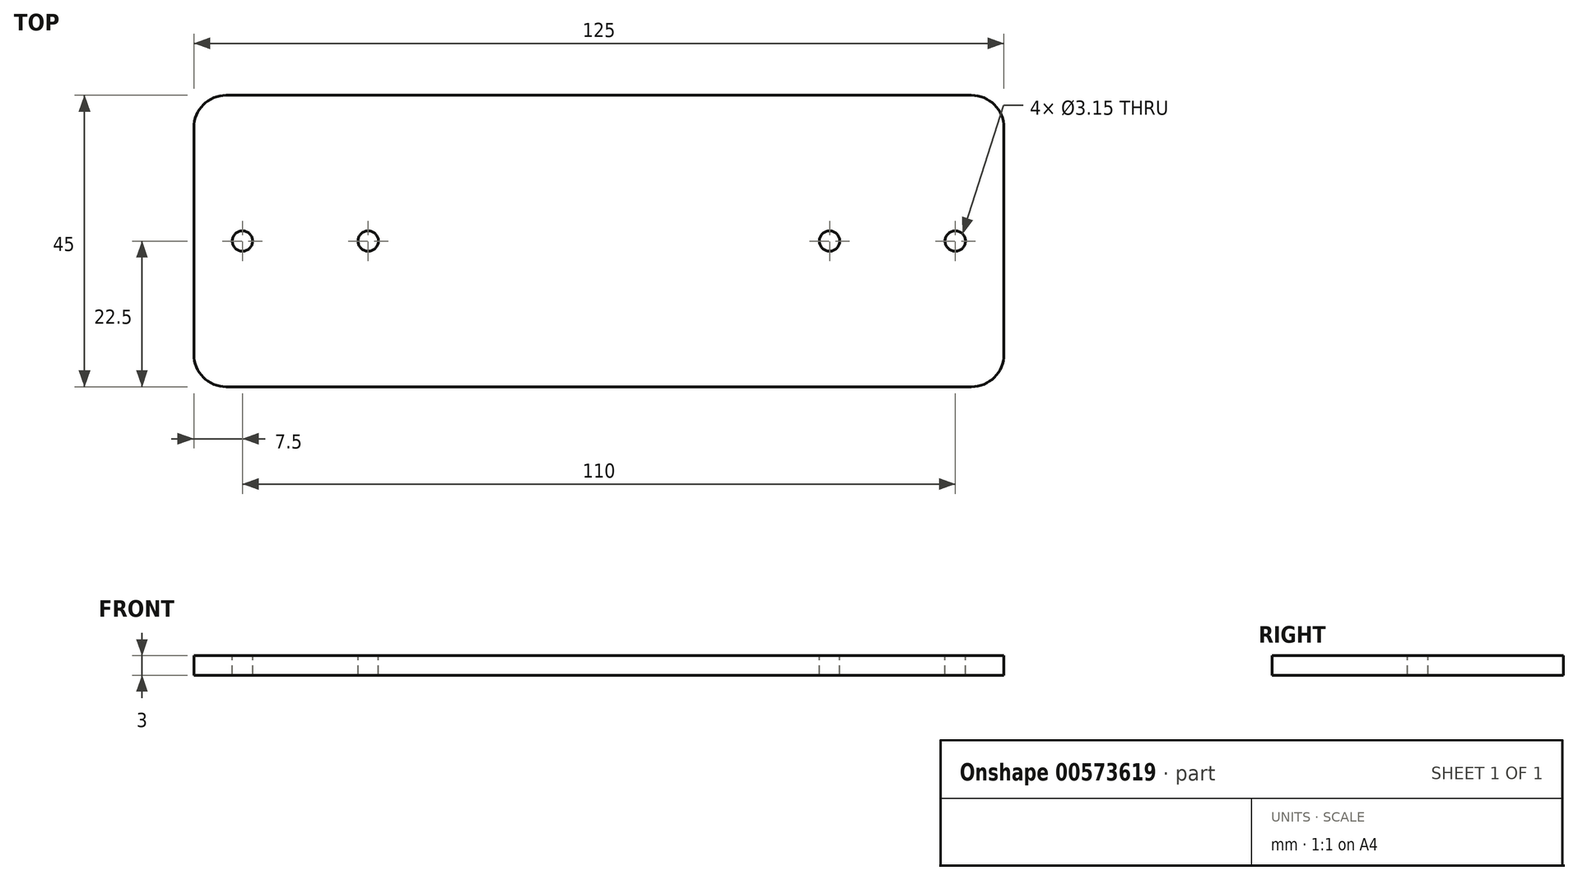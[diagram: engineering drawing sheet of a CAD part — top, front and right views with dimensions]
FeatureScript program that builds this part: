
annotation { "Feature Type Name" : "Feature", "Feature Type Description" : "" }
export const myFeature = defineFeature(function(context is Context, id is Id, definition is map)
    precondition{}
    {
        {
            var Q0;
            Q0=qCreatedBy(makeId("Top.planeOp"),FACE);
            var sketch = newSketch(context, id + "F0", { "sketchPlane" : qUnion([Q0])});
            skLineSegment(sketch, "E0.bottom", {"start": v(62.5, -22.5) * mm, "end": v(-62.5, -22.5) * mm});
            skLineSegment(sketch, "E0.top", {"start": v(62.5, 22.5) * mm, "end": v(-62.5, 22.5) * mm});
            skLineSegment(sketch, "E0.left", {"start": v(62.5, -22.5) * mm, "end": v(62.5, 22.5) * mm});
            skLineSegment(sketch, "E0.right", {"start": v(-62.5, -22.5) * mm, "end": v(-62.5, 22.5) * mm});
            skPoint(sketch, "E0.middle", {"position": v(0, 0) * mm});
            skSolve(sketch);
        }
        {
            var Q0;
            Q0 = qSketchRegion(id + "F0", true);
            extrude(context, id + "F1", {"entities" : qUnion([Q0]), "depth" : 3 * mm, "offsetDistance" : 25 * mm});
        }
        {
            var Q0;
            Q0=makeQuery(id+"F1.opExtrude","CAP_FACE",FACE,{"disambiguationData":[OSD([sQuery(id+"F0.wireOp",EDGE,"E0.bottom"),sQuery(id+"F0.wireOp",EDGE,"E0.top"),sQuery(id+"F0.wireOp",EDGE,"E0.left"),sQuery(id+"F0.wireOp",EDGE,"E0.right")])],"isStart":false});
            var sketch = newSketch(context, id + "F2", { "sketchPlane" : qUnion([Q0])});
            skLineSegment(sketch, "E1.bottom", {"start": v(-50.8, 22.5) * mm, "end": v(-37.8, 22.5) * mm});
            skLineSegment(sketch, "E1.top", {"start": v(-50.8, -22.5) * mm, "end": v(-37.8, -22.5) * mm});
            skLineSegment(sketch, "E1.left", {"start": v(-50.8, 22.5) * mm, "end": v(-50.8, -22.5) * mm});
            skLineSegment(sketch, "E1.right", {"start": v(-37.8, 22.5) * mm, "end": v(-37.8, -22.5) * mm});
            skLineSegment(sketch, "E2.bottom", {"start": v(37.8, 22.5) * mm, "end": v(50.8, 22.5) * mm});
            skLineSegment(sketch, "E2.top", {"start": v(37.8, -22.5) * mm, "end": v(50.8, -22.5) * mm});
            skLineSegment(sketch, "E2.left", {"start": v(37.8, 22.5) * mm, "end": v(37.8, -22.5) * mm});
            skLineSegment(sketch, "E2.right", {"start": v(50.8, 22.5) * mm, "end": v(50.8, -22.5) * mm});
            skLineSegment(sketch, "E3", {"start": v(-37.8, 0) * mm, "end": v(37.8, 0) * mm, "construction": true});
            skPoint(sketch, "E4", {"position": v(0, 0) * mm});
            skLineSegment(sketch, "E5", {"start": v(0, 22.5) * mm, "end": v(0, -22.5) * mm, "construction": true});
            skPoint(sketch, "E6", {"position": v(0, -22.5) * mm});
            skSolve(sketch);
        }
        {
            var Q0;
            {var subQ0=sQuery(id+"F2.wireOp",EDGE,"E1.right");Q0=makeQuery(id+"F2.imprint","IMPRINT",FACE,{"disambiguationData":[TD([[makeQuery(id+"F2.imprint","IMPRINT",EDGE,{"derivedFrom":subQ0}),1.0]])]});}
            var sketch = newSketch(context, id + "F3", { "sketchPlane" : qUnion([Q0])});
            skCircle(sketch, "E7", {"center": v(-55, 0) * mm, "radius": 1.57 * mm});
            skCircle(sketch, "E8", {"center": v(-35.6, 0) * mm, "radius": 1.57 * mm});
            skLineSegment(sketch, "E9", {"start": v(-55, 0) * mm, "end": v(-35.6, 0) * mm, "construction": true});
            skLineSegment(sketch, "E10", {"start": v(-45.3, 22.5) * mm, "end": v(-45.3, -22.5) * mm, "construction": true});
            skPoint(sketch, "E11", {"position": v(-45.3, 0) * mm});
            skPoint(sketch, "E11.positionSnap0", {"position": v(-45.3, 0) * mm});
            skCircle(sketch, "E12", {"center": v(-55, 0) * mm, "radius": 2.2 * mm, "construction": true});
            skCircle(sketch, "E13", {"center": v(-35.6, 0) * mm, "radius": 2.2 * mm, "construction": true});
            skLineSegment(sketch, "E14", {"start": v(0, 22.63) * mm, "end": v(0, -22.3) * mm, "construction": true});
            skPoint(sketch, "E15.MirrorP", {"position": v(45.3, 0) * mm});
            skCircle(sketch, "E16.MirrorC", {"center": v(55, 0) * mm, "radius": 1.57 * mm});
            skCircle(sketch, "E17.MirrorC", {"center": v(35.6, 0) * mm, "radius": 1.57 * mm});
            skLineSegment(sketch, "E18.MirrorCS", {"start": v(45.3, 22.5) * mm, "end": v(45.3, -22.5) * mm, "construction": true});
            skLineSegment(sketch, "E19.MirrorCS", {"start": v(55, 0) * mm, "end": v(35.6, 0) * mm, "construction": true});
            skCircle(sketch, "E20.MirrorC", {"center": v(55, 0) * mm, "radius": 2.2 * mm, "construction": true});
            skCircle(sketch, "E21.MirrorC", {"center": v(35.6, 0) * mm, "radius": 2.2 * mm, "construction": true});
            skSolve(sketch);
        }
        {
            var Q0;
            Q0 = qSketchRegion(id + "F3", true);
            var Q1;
            Q1=makeQuery(id+"F1.opExtrude","CAP_FACE",FACE,{"disambiguationData":[OSD([sQuery(id+"F0.wireOp",EDGE,"E0.bottom"),sQuery(id+"F0.wireOp",EDGE,"E0.top"),sQuery(id+"F0.wireOp",EDGE,"E0.left"),sQuery(id+"F0.wireOp",EDGE,"E0.right")])],"isStart":true});
            extrude(context, id + "F4", {"entities" : qUnion([Q0]), "operationType" : NewBodyOperationType.REMOVE, "endBound" : BoundingType.UP_TO_SURFACE, "oppositeDirection" : true, "depth" : 25 * mm, "endBoundEntityFace" : qUnion([Q1]), "offsetDistance" : 25 * mm});
        }
        {
            var Q0;
            Q0=makeQuery(id+"F1.opExtrude","SWEPT_EDGE",EDGE,{"disambiguationData":[OSD([sQuery(id+"F0.wireOp",EDGE,"E0.bottom"),sQuery(id+"F0.wireOp",EDGE,"E0.right")])]});
            var Q1;
            Q1=makeQuery(id+"F1.opExtrude","SWEPT_EDGE",EDGE,{"disambiguationData":[OSD([sQuery(id+"F0.wireOp",EDGE,"E0.bottom"),sQuery(id+"F0.wireOp",EDGE,"E0.left")])]});
            var Q2;
            Q2=makeQuery(id+"F1.opExtrude","SWEPT_EDGE",EDGE,{"disambiguationData":[OSD([sQuery(id+"F0.wireOp",EDGE,"E0.top"),sQuery(id+"F0.wireOp",EDGE,"E0.left")])]});
            var Q3;
            Q3=makeQuery(id+"F1.opExtrude","SWEPT_EDGE",EDGE,{"disambiguationData":[OSD([sQuery(id+"F0.wireOp",EDGE,"E0.top"),sQuery(id+"F0.wireOp",EDGE,"E0.right")])]});
            fillet(context, id + "F5", {"entities" : qUnion([Q0, Q1, Q2, Q3]), "radius" : 5 * mm, "tangentPropagation" : true, "allowEdgeOverflow" : false});
        }
    });
